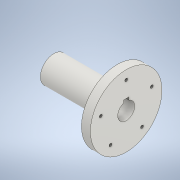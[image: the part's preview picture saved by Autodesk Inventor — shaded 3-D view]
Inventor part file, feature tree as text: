
AUTODESK INVENTOR PART (.ipt)
format: ipt  version: 2022.1 (Build 261234000, 234)  size: 152,064 bytes
history: native  units: mm
features: sketch x4, extrude x3, other x1, hole x1, projected_geometry x1
ambient origin geometry x8: Origin, YZ Plane, XZ Plane, XY Plane, X Axis, Y Axis, Z Axis, Center Point
bodies: Body1 (feature_tree)
feature tree (10):
  other  "Sólido1"
  extrude  "Extrusión1"  Depth=60.0mm
  extrude  "Extrusión2"  Depth=12.566371mm
  extrude  "Extrusión3"  Depth=12.566371mm
  hole  "Agujero1"  [1 undecoded]
  sketch  "Boceto1"  dims[d0=80.0mm d1=60.0mm]
  sketch  "Boceto2"  dims[d7=12.566371mm d8=12.566371mm]
  sketch  "Boceto3"  dims[d9=12.566371mm d10=12.566371mm]
  sketch  "Boceto4"  dims[d12=10.0mm d13=0.0mm d14=30.0mm d15=71.0mm d16=0.0mm d17=19.0mm d18=6.0mm d19=12.0mm d20=12.0mm d21=3.0mm d22=0.0mm d23=0.0mm d24=2.5mm d25=3.242mm d26=8.0mm d27=4.0mm d28=2.0mm d29=90.0deg d30=8.0mm d31=20.594885mm]
  projected_geometry  "Contorno proyectado1"
note: 1 required parameter value undecoded (feature->parameter linkage not recoverable at this tier; creation-order binding heuristic only, values carry confidence <= 0.55)
